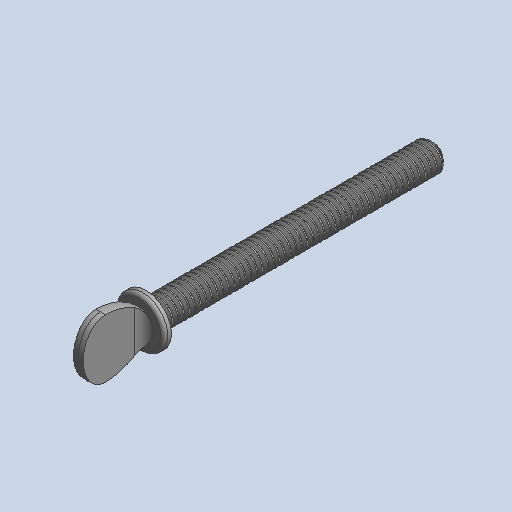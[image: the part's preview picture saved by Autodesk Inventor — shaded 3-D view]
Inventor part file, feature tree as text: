
AUTODESK INVENTOR PART (.ipt)
format: ipt  version: 2022.3 (Build 263350000, 350)  size: 873,984 bytes
history: native  units: mm (DEFAULTED — no unit token found)
features: fillet x1
ambient origin geometry x8: Origin, YZ Plane, XZ Plane, XY Plane, X Axis, Y Axis, Z Axis, Center Point
bodies: Solid1 (feature_tree)
feature tree (1):
  fillet  "Fillet14"  [1 undecoded]
note: 1 required parameter value undecoded (feature->parameter linkage not recoverable at this tier; creation-order binding heuristic only, values carry confidence <= 0.55)
